# Revit family: HOB_GEN_SilhouetteSlatted
name_source: partatom
category: Generic Models
units: mm (PartAtom-declared; Revit-internal decimal feet)

## family parameters
Always vertical = Yes
Can host rebar = No
Cut with Voids When Loaded = No
Maintain Annotation Orientation = No
Part Type = Normal
Room Calculation Point = No
Round Connector Dimension = Use Diameter
Shared = Yes
Work Plane-Based = No

## types (1)
- SilhouetteSlatted_W540xH2330
    BattenDepth = 20 mm  [stored 0.0656168 ft]
    BattenSpacing = 34 mm
    BattenWidth = 20 mm  [stored 0.0656168 ft]
    Battens Material = Bamboo_horizontalGrain
    BattensBottomOffset = 0 mm  [stored 0 ft]
    BattensTopOffset = 0 mm  [stored 0 ft]
    Cost = 286 $
    Default Elevation = 0 mm  [stored 0 ft]
    Description = 17x35 mm slat / 540/750 mm standard width / 2330/2650 mm Standard height
    Manufacturer = HOB
    MaxHeight = 1800 mm  [stored 5.90551 ft]
    MaxWidth = 705 mm  [stored 2.31299 ft]
    Model = Silhouette Slatted
    PanelCost = 300 $
    RailBottomOffset = 50 mm  [stored 0.164042 ft]
    RailTopOffset = 50 mm  [stored 0.164042 ft]
    SideOffset = 17 mm  [stored 0.0557743 ft]
    Support Rail Material = HOB_Black
    URL = https://houseofbamboo.com.au

note: [stored X ft] marks values corroborated as IEEE doubles in the binary element streams (Revit-internal decimal feet)

## geometry (parser evidence)
native form markers: Sweep x10
no freeform markers — native parametric forms only
